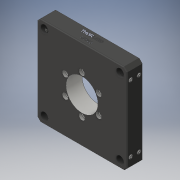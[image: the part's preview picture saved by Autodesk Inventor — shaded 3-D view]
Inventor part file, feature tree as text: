
AUTODESK INVENTOR PART (.ipt)
format: ipt  version: 2016 (Build 200138000, 138)  size: 1,047,552 bytes
history: native  units: in
note: dims shown in document units (in); Inventor stores cm internally (conversion verified against a paired STEP export)
features: other x9, sketch x5, projected_geometry x3, extrude x2, hole x1, pattern_circular x1
ambient origin geometry x8: Origin, YZ Plane, XZ Plane, XY Plane, X Axis, Y Axis, Z Axis, Center Point
bodies: Solid1 (feature_tree), Solid2 (feature_tree), Solid3 (feature_tree), Solid4 (feature_tree), Solid5 (feature_tree), Solid6 (feature_tree), Solid7 (feature_tree), Solid8 (feature_tree), Solid9 (feature_tree)
feature tree (21):
  extrude  "Extrusion1"  Depth=1.0in
  extrude  "Extrusion2"  Depth=1.0in
  hole  "Hole1"  [1 undecoded]
  pattern_circular  "Circular Pattern1"  [2 undecoded]
  sketch  "Sketch1"  dims[d0=1.0in d1=0.0in d2=1.0in]
  sketch  "Sketch5"
  projected_geometry  "Projected Loop1"
  projected_geometry  "Projected Loop2"
  sketch  "Sketch2"  dims[d3=1.0in d4=0.0in d5=1.204in]
  sketch  "Sketch3"  dims[d6=2.3622in d8=0.0in]
  sketch  "Sketch4"  dims[d10=0.096in d11=0.75in d12=0.188in d13=0.086in d14=0.563in d15=1.0in d16=0.8108in d17=2.3622in d18=2.4737in]
  projected_geometry  "Projected Loop3"
  other  "13107-001-1-solid1"
  other  "SS4S019-1-1-solid1"
  other  "SS4S019-1-2-solid1"
  other  "SS4S019-1-3-solid1"
  other  "SS4S019-1-4-solid1"
  other  "SS4S019-1-5-solid1"
  other  "SS4S019-1-6-solid1"
  other  "SS4S019-1-7-solid1"
  other  "SS4S019-1-8-solid1"
note: 3 required parameter values undecoded (feature->parameter linkage not recoverable at this tier; creation-order binding heuristic only, values carry confidence <= 0.55)
